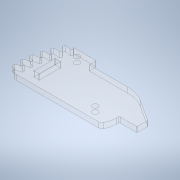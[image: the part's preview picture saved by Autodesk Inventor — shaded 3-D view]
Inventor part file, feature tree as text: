
AUTODESK INVENTOR PART (.ipt)
format: ipt  version: 2021 (Build 250183000, 183)  size: 243,200 bytes
history: native  units: mm
features: extrude x1, sketch x1
ambient origin geometry x8: Origin, YZ Plane, XZ Plane, XY Plane, X Axis, Y Axis, Z Axis, Center Point
bodies: Solid1 (feature_tree)
feature tree (2):
  extrude  "Extrusion1"  Depth=0.5mm
  sketch  "Sketch1"  dims[d0=0.5mm d2=0.5mm d4=3.0mm d5=0.0mm d17=5.759587mm d18=5.759587mm d19=38.625mm d20=35.0mm d21=3.2mm d22=6.75mm d24=2.0mm d25=2.0mm d26=0.5mm d27=0.25mm d28=34.5mm d30=0.01mm d31=0.25mm d32=0.25mm d33=0.25mm d34=0.25mm d39=6.75mm d40=6.65mm d41=12.65mm d43=12.0mm d44=3.0mm d45=21.772899mm d46=29.35347mm d56=25.2mm d57=25.25mm]
